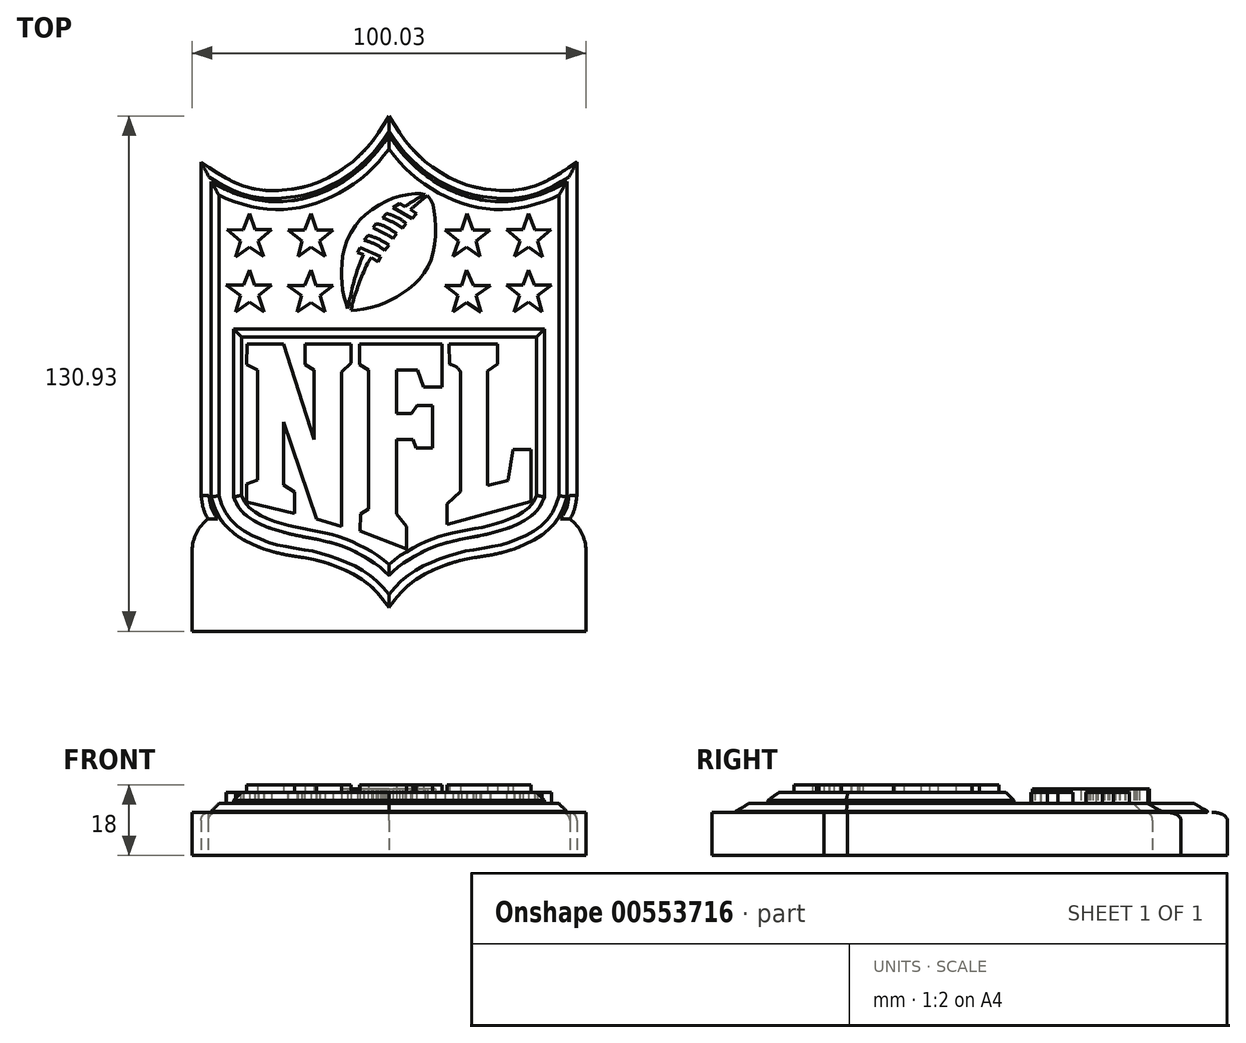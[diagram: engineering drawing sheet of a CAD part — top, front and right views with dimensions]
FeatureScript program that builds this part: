
annotation { "Feature Type Name" : "Feature", "Feature Type Description" : "" }
export const myFeature = defineFeature(function(context is Context, id is Id, definition is map)
    precondition{}
    {
        {
            var Q0;
            Q0=qCreatedBy(makeId("Top.planeOp"),FACE);
            var sketch = newSketch(context, id + "F0", { "sketchPlane" : qUnion([Q0])});
            skLineSegment(sketch, "E0", {"start": v(50, 132.63) * mm, "end": v(50, 0) * mm, "construction": true});
            skLineSegment(sketch, "E1", {"start": v(0, 66.31) * mm, "end": v(100, 66.31) * mm, "construction": true});
            skLineSegment(sketch, "E2", {"start": v(2.28, 119.14) * mm, "end": v(2.28, 34.43) * mm});
            skFitSpline(sketch, "E3", {"points": [v(2.28, 34.43) * mm, v(2.7, 31.8) * mm, v(3.9, 28.8) * mm, v(6.54, 25.06) * mm, v(6.72, 24.8) * mm, v(11.59, 20.83) * mm, v(18.84, 17.77) * mm, v(25.54, 16.2) * mm, v(30.8, 15.28) * mm, v(36.61, 13.45) * mm, v(42.89, 9.8) * mm, v(47.24, 5.22) * mm, v(49.83, 1.28) * mm], "startDerivative": vector(5.68, -43.12) * mm, "endDerivative": vector(28.67, -47.03) * mm});
            skFitSpline(sketch, "E4", {"points": [v(2.28, 119.14) * mm, v(6.14, 116.65) * mm, v(11.7, 113.64) * mm, v(17.48, 112.13) * mm, v(24.37, 112.19) * mm, v(31.61, 113.93) * mm, v(38.21, 117.4) * mm, v(43.13, 121.5) * mm, v(46.78, 125.85) * mm, v(50, 130.93) * mm], "startDerivative": vector(38.47, -25.35) * mm, "endDerivative": vector(28.8, 47.95) * mm});
            skFitSpline(sketch, "E5.MirrorCS", {"points": [v(97.72, 119.14) * mm, v(93.86, 116.65) * mm, v(88.3, 113.64) * mm, v(82.52, 112.13) * mm, v(75.63, 112.19) * mm, v(68.39, 113.93) * mm, v(61.79, 117.4) * mm, v(56.87, 121.5) * mm, v(53.22, 125.85) * mm, v(50, 130.93) * mm], "startDerivative": vector(-38.47, -25.35) * mm, "endDerivative": vector(-28.8, 47.95) * mm});
            skLineSegment(sketch, "E6.MirrorCS", {"start": v(97.72, 119.14) * mm, "end": v(97.72, 34.43) * mm});
            skFitSpline(sketch, "E7.MirrorCS", {"points": [v(97.72, 34.43) * mm, v(97.3, 31.8) * mm, v(96.1, 28.8) * mm, v(93.46, 25.06) * mm, v(93.28, 24.8) * mm, v(88.41, 20.83) * mm, v(81.16, 17.77) * mm, v(74.46, 16.2) * mm, v(69.2, 15.28) * mm, v(63.39, 13.45) * mm, v(57.11, 9.8) * mm, v(52.76, 5.22) * mm, v(50.17, 1.28) * mm], "startDerivative": vector(-5.68, -43.12) * mm, "endDerivative": vector(-28.67, -47.03) * mm});
            skLineSegment(sketch, "E8", {"start": v(49.83, 1.28) * mm, "end": v(50.17, 1.28) * mm});
            skSolve(sketch);
        }
        {
            var Q0;
            Q0=qSketchRegion(id+"F0",true);
            extrude(context, id + "F1", {"entities" : qUnion([Q0]), "depth" : 11 * mm, "offsetDistance" : 25 * mm});
        }
        {
            var Q0;
            Q0=qCreatedBy(makeId("Top.planeOp"),FACE);
            var sketch = newSketch(context, id + "F2", { "sketchPlane" : qUnion([Q0])});
            skLineSegment(sketch, "E9", {"start": v(4.81, 114.27) * mm, "end": v(4.81, 34.15) * mm});
            skFitSpline(sketch, "E10", {"points": [v(4.81, 34.15) * mm, v(5.59, 31.7) * mm, v(7.24, 28.39) * mm, v(9.58, 25.71) * mm, v(13.14, 23.2) * mm, v(19.38, 20.53) * mm, v(25.14, 19.21) * mm, v(30.66, 18.27) * mm, v(36.62, 16.45) * mm, v(42.35, 13.69) * mm, v(46.76, 10.07) * mm, v(50, 6.03) * mm], "startDerivative": vector(10.12, -36.02) * mm, "endDerivative": vector(32.83, -44.73) * mm});
            skFitSpline(sketch, "E11", {"points": [v(4.81, 114.27) * mm, v(9.5, 111.76) * mm, v(18.69, 109.31) * mm, v(27.27, 109.72) * mm, v(36.46, 113.13) * mm, v(44.77, 119.4) * mm, v(49.95, 125.93) * mm], "startDerivative": vector(31.76, -19.44) * mm, "endDerivative": vector(28.45, 40.4) * mm});
            skFitSpline(sketch, "E12.MirrorCS", {"points": [v(95.19, 114.27) * mm, v(90.5, 111.76) * mm, v(81.31, 109.31) * mm, v(72.73, 109.72) * mm, v(63.54, 113.13) * mm, v(55.23, 119.4) * mm, v(50.05, 125.93) * mm], "startDerivative": vector(-31.76, -19.44) * mm, "endDerivative": vector(-28.45, 40.4) * mm});
            skLineSegment(sketch, "E13.MirrorCS", {"start": v(95.19, 114.27) * mm, "end": v(95.19, 34.15) * mm});
            skFitSpline(sketch, "E14.MirrorCS", {"points": [v(95.19, 34.15) * mm, v(94.41, 31.7) * mm, v(92.76, 28.39) * mm, v(90.42, 25.71) * mm, v(86.86, 23.2) * mm, v(80.62, 20.53) * mm, v(74.86, 19.21) * mm, v(69.34, 18.27) * mm, v(63.38, 16.45) * mm, v(57.65, 13.69) * mm, v(53.24, 10.07) * mm, v(50, 6.03) * mm], "startDerivative": vector(-10.12, -36.02) * mm, "endDerivative": vector(-32.83, -44.73) * mm});
            skLineSegment(sketch, "E15", {"start": v(50, 6.03) * mm, "end": v(50, 6.03) * mm});
            skLineSegment(sketch, "E16", {"start": v(49.95, 125.93) * mm, "end": v(50.05, 125.93) * mm});
            skSolve(sketch);
        }
        {
            var Q0;
            Q0=qSketchRegion(id+"F2",true);
            extrude(context, id + "F3", {"entities" : qUnion([Q0]), "operationType" : NewBodyOperationType.ADD, "depth" : 13.2 * mm, "offsetDistance" : 25 * mm});
        }
        {
            var Q0;
            Q0=makeQuery(id+"F1.opExtrude","CAP_EDGE",EDGE,{"disambiguationData":[OSD([sQuery(id+"F0.wireOp",EDGE,"E2")])],"isStart":false});
            var Q1;
            Q1=makeQuery(id+"F1.opExtrude","CAP_EDGE",EDGE,{"disambiguationData":[OSD([sQuery(id+"F0.wireOp",EDGE,"E4")])],"isStart":false});
            var Q2;
            Q2=makeQuery(id+"F1.opExtrude","CAP_EDGE",EDGE,{"disambiguationData":[OSD([sQuery(id+"F0.wireOp",EDGE,"E5.MirrorCS")])],"isStart":false});
            var Q3;
            Q3=makeQuery(id+"F1.opExtrude","CAP_EDGE",EDGE,{"disambiguationData":[OSD([sQuery(id+"F0.wireOp",EDGE,"E6.MirrorCS")])],"isStart":false});
            var Q4;
            Q4=makeQuery(id+"F1.opExtrude","CAP_EDGE",EDGE,{"disambiguationData":[OSD([sQuery(id+"F0.wireOp",EDGE,"E7.MirrorCS")])],"isStart":false});
            var Q5;
            Q5=makeQuery(id+"F1.opExtrude","CAP_EDGE",EDGE,{"disambiguationData":[OSD([sQuery(id+"F0.wireOp",EDGE,"E3")])],"isStart":false});
            fillet(context, id + "F4", {"entities" : qUnion([Q0, Q1, Q2, Q3, Q4, Q5]), "radius" : 2 * mm, "tangentPropagation" : true, "allowEdgeOverflow" : false});
        }
        {
            var Q0;
            Q0=qCreatedBy(makeId("Top.planeOp"),FACE);
            var sketch = newSketch(context, id + "F5", { "sketchPlane" : qUnion([Q0])});
            skLineSegment(sketch, "E17", {"start": v(12.94, 101.93) * mm, "end": v(14.6, 106.09) * mm});
            skLineSegment(sketch, "E18", {"start": v(14.6, 106.09) * mm, "end": v(16, 102) * mm});
            skLineSegment(sketch, "E19", {"start": v(16, 102) * mm, "end": v(20.2, 102) * mm});
            skLineSegment(sketch, "E20", {"start": v(20.2, 102) * mm, "end": v(16.73, 99.2) * mm});
            skLineSegment(sketch, "E21", {"start": v(16.73, 99.2) * mm, "end": v(18.1, 95.2) * mm});
            skLineSegment(sketch, "E22", {"start": v(18.1, 95.2) * mm, "end": v(14.6, 97.61) * mm});
            skLineSegment(sketch, "E23", {"start": v(14.6, 97.61) * mm, "end": v(11.02, 95.08) * mm});
            skLineSegment(sketch, "E24", {"start": v(11.02, 95.08) * mm, "end": v(12.25, 99.2) * mm});
            skLineSegment(sketch, "E25", {"start": v(12.25, 99.2) * mm, "end": v(8.8, 102) * mm});
            skLineSegment(sketch, "E26", {"start": v(8.8, 102) * mm, "end": v(12.94, 101.93) * mm});
            skLineSegment(sketch, "E27", {"start": v(28.6, 101.93) * mm, "end": v(30.15, 106.09) * mm});
            skLineSegment(sketch, "E28", {"start": v(30.15, 106.09) * mm, "end": v(31.57, 101.93) * mm});
            skLineSegment(sketch, "E29", {"start": v(31.57, 101.93) * mm, "end": v(35.75, 101.93) * mm});
            skLineSegment(sketch, "E30", {"start": v(35.75, 101.93) * mm, "end": v(32.38, 99.2) * mm});
            skLineSegment(sketch, "E31", {"start": v(32.38, 99.2) * mm, "end": v(33.75, 95.2) * mm});
            skLineSegment(sketch, "E32", {"start": v(33.75, 95.2) * mm, "end": v(30.26, 97.61) * mm});
            skLineSegment(sketch, "E33", {"start": v(30.26, 97.61) * mm, "end": v(26.9, 95.23) * mm});
            skLineSegment(sketch, "E34", {"start": v(26.9, 95.23) * mm, "end": v(27.86, 99.2) * mm});
            skLineSegment(sketch, "E35", {"start": v(27.86, 99.2) * mm, "end": v(24.4, 101.93) * mm});
            skLineSegment(sketch, "E36", {"start": v(24.4, 101.93) * mm, "end": v(28.6, 101.93) * mm});
            skLineSegment(sketch, "E37", {"start": v(14.6, 91.77) * mm, "end": v(15.9, 87.96) * mm});
            skLineSegment(sketch, "E38", {"start": v(15.9, 87.96) * mm, "end": v(20.12, 87.96) * mm});
            skLineSegment(sketch, "E39", {"start": v(20.12, 87.96) * mm, "end": v(16.82, 85.26) * mm});
            skLineSegment(sketch, "E40", {"start": v(16.82, 85.26) * mm, "end": v(18.25, 81.05) * mm});
            skLineSegment(sketch, "E41", {"start": v(18.25, 81.05) * mm, "end": v(14.6, 83.58) * mm});
            skLineSegment(sketch, "E42", {"start": v(14.6, 83.58) * mm, "end": v(11.08, 81.12) * mm});
            skLineSegment(sketch, "E43", {"start": v(11.08, 81.12) * mm, "end": v(12.33, 85.26) * mm});
            skLineSegment(sketch, "E44", {"start": v(12.33, 85.26) * mm, "end": v(8.66, 87.96) * mm});
            skLineSegment(sketch, "E45", {"start": v(8.66, 87.96) * mm, "end": v(13, 87.96) * mm});
            skLineSegment(sketch, "E46", {"start": v(13, 87.96) * mm, "end": v(14.6, 91.77) * mm});
            skLineSegment(sketch, "E47", {"start": v(30.26, 91.71) * mm, "end": v(31.53, 87.83) * mm});
            skLineSegment(sketch, "E48", {"start": v(31.53, 87.83) * mm, "end": v(35.8, 87.83) * mm});
            skLineSegment(sketch, "E49", {"start": v(35.8, 87.83) * mm, "end": v(32.42, 85.26) * mm});
            skLineSegment(sketch, "E50", {"start": v(32.42, 85.26) * mm, "end": v(33.78, 81.05) * mm});
            skLineSegment(sketch, "E51", {"start": v(33.78, 81.05) * mm, "end": v(30.26, 83.49) * mm});
            skLineSegment(sketch, "E52", {"start": v(30.26, 83.49) * mm, "end": v(26.68, 81.07) * mm});
            skLineSegment(sketch, "E53", {"start": v(26.68, 81.07) * mm, "end": v(27.84, 85.26) * mm});
            skLineSegment(sketch, "E54", {"start": v(27.84, 85.26) * mm, "end": v(24.2, 87.79) * mm});
            skLineSegment(sketch, "E55", {"start": v(24.2, 87.79) * mm, "end": v(28.58, 87.79) * mm});
            skLineSegment(sketch, "E56", {"start": v(28.58, 87.79) * mm, "end": v(30.26, 91.71) * mm});
            skLineSegment(sketch, "E57.MirrorCS", {"start": v(69.74, 91.71) * mm, "end": v(68.47, 87.83) * mm});
            skLineSegment(sketch, "E58.MirrorCS", {"start": v(68.47, 87.83) * mm, "end": v(64.2, 87.83) * mm});
            skLineSegment(sketch, "E59.MirrorCS", {"start": v(64.2, 87.83) * mm, "end": v(67.58, 85.26) * mm});
            skLineSegment(sketch, "E60.MirrorCS", {"start": v(67.58, 85.26) * mm, "end": v(66.22, 81.05) * mm});
            skLineSegment(sketch, "E61.MirrorCS", {"start": v(66.22, 81.05) * mm, "end": v(69.74, 83.49) * mm});
            skLineSegment(sketch, "E62.MirrorCS", {"start": v(69.74, 83.49) * mm, "end": v(73.32, 81.07) * mm});
            skLineSegment(sketch, "E63.MirrorCS", {"start": v(73.32, 81.07) * mm, "end": v(72.16, 85.26) * mm});
            skLineSegment(sketch, "E64.MirrorCS", {"start": v(72.16, 85.26) * mm, "end": v(75.8, 87.79) * mm});
            skLineSegment(sketch, "E65.MirrorCS", {"start": v(75.8, 87.79) * mm, "end": v(71.42, 87.79) * mm});
            skLineSegment(sketch, "E66.MirrorCS", {"start": v(71.42, 87.79) * mm, "end": v(69.74, 91.71) * mm});
            skLineSegment(sketch, "E67.MirrorCS", {"start": v(69.85, 106.09) * mm, "end": v(68.43, 101.93) * mm});
            skLineSegment(sketch, "E68.MirrorCS", {"start": v(71.4, 101.93) * mm, "end": v(69.85, 106.09) * mm});
            skLineSegment(sketch, "E69.MirrorCS", {"start": v(75.6, 101.93) * mm, "end": v(71.4, 101.93) * mm});
            skLineSegment(sketch, "E70.MirrorCS", {"start": v(72.14, 99.2) * mm, "end": v(75.6, 101.93) * mm});
            skLineSegment(sketch, "E71.MirrorCS", {"start": v(73.1, 95.23) * mm, "end": v(72.14, 99.2) * mm});
            skLineSegment(sketch, "E72.MirrorCS", {"start": v(69.74, 97.61) * mm, "end": v(73.1, 95.23) * mm});
            skLineSegment(sketch, "E73.MirrorCS", {"start": v(66.25, 95.2) * mm, "end": v(69.74, 97.61) * mm});
            skLineSegment(sketch, "E74.MirrorCS", {"start": v(67.62, 99.2) * mm, "end": v(66.25, 95.2) * mm});
            skLineSegment(sketch, "E75.MirrorCS", {"start": v(64.25, 101.93) * mm, "end": v(67.62, 99.2) * mm});
            skLineSegment(sketch, "E76.MirrorCS", {"start": v(68.43, 101.93) * mm, "end": v(64.25, 101.93) * mm});
            skLineSegment(sketch, "E77.MirrorCS", {"start": v(85.4, 106.09) * mm, "end": v(84, 102) * mm});
            skLineSegment(sketch, "E78.MirrorCS", {"start": v(87.06, 101.93) * mm, "end": v(85.4, 106.09) * mm});
            skLineSegment(sketch, "E79.MirrorCS", {"start": v(91.2, 102) * mm, "end": v(87.06, 101.93) * mm});
            skLineSegment(sketch, "E80.MirrorCS", {"start": v(87.75, 99.2) * mm, "end": v(91.2, 102) * mm});
            skLineSegment(sketch, "E81.MirrorCS", {"start": v(88.98, 95.08) * mm, "end": v(87.75, 99.2) * mm});
            skLineSegment(sketch, "E82.MirrorCS", {"start": v(85.4, 97.61) * mm, "end": v(88.98, 95.08) * mm});
            skLineSegment(sketch, "E83.MirrorCS", {"start": v(81.9, 95.2) * mm, "end": v(85.4, 97.61) * mm});
            skLineSegment(sketch, "E84.MirrorCS", {"start": v(83.27, 99.2) * mm, "end": v(81.9, 95.2) * mm});
            skLineSegment(sketch, "E85.MirrorCS", {"start": v(79.8, 102) * mm, "end": v(83.27, 99.2) * mm});
            skLineSegment(sketch, "E86.MirrorCS", {"start": v(84, 102) * mm, "end": v(79.8, 102) * mm});
            skLineSegment(sketch, "E87.MirrorCS", {"start": v(85.4, 91.77) * mm, "end": v(84.1, 87.96) * mm});
            skLineSegment(sketch, "E88.MirrorCS", {"start": v(87, 87.96) * mm, "end": v(85.4, 91.77) * mm});
            skLineSegment(sketch, "E89.MirrorCS", {"start": v(91.34, 87.96) * mm, "end": v(87, 87.96) * mm});
            skLineSegment(sketch, "E90.MirrorCS", {"start": v(87.67, 85.26) * mm, "end": v(91.34, 87.96) * mm});
            skLineSegment(sketch, "E91.MirrorCS", {"start": v(88.92, 81.12) * mm, "end": v(87.67, 85.26) * mm});
            skLineSegment(sketch, "E92.MirrorCS", {"start": v(85.4, 83.58) * mm, "end": v(88.92, 81.12) * mm});
            skLineSegment(sketch, "E93.MirrorCS", {"start": v(81.75, 81.05) * mm, "end": v(85.4, 83.58) * mm});
            skLineSegment(sketch, "E94.MirrorCS", {"start": v(83.18, 85.26) * mm, "end": v(81.75, 81.05) * mm});
            skLineSegment(sketch, "E95.MirrorCS", {"start": v(79.88, 87.96) * mm, "end": v(83.18, 85.26) * mm});
            skLineSegment(sketch, "E96.MirrorCS", {"start": v(84.1, 87.96) * mm, "end": v(79.88, 87.96) * mm});
            skLineSegment(sketch, "E97", {"start": v(10.5, 76.74) * mm, "end": v(49.97, 76.74) * mm});
            skPoint(sketch, "E97.startSnap0", {"position": v(10.5, 86.61) * mm});
            skLineSegment(sketch, "E98", {"start": v(10.5, 76.74) * mm, "end": v(10.5, 34.11) * mm});
            skFitSpline(sketch, "E99", {"points": [v(10.5, 34.11) * mm, v(12.27, 30.84) * mm, v(16.58, 27.57) * mm, v(24.85, 24.72) * mm, v(31.63, 23.36) * mm, v(39.01, 21.26) * mm, v(46.72, 17.05) * mm, v(49.97, 14.22) * mm], "startDerivative": vector(13.37, -30.84) * mm, "endDerivative": vector(23.65, -23.25) * mm});
            skLineSegment(sketch, "E100.MirrorCS", {"start": v(89.5, 76.74) * mm, "end": v(50.03, 76.74) * mm});
            skLineSegment(sketch, "E101.MirrorCS", {"start": v(89.5, 76.74) * mm, "end": v(89.5, 34.11) * mm});
            skFitSpline(sketch, "E102.MirrorCS", {"points": [v(89.5, 34.11) * mm, v(87.73, 30.84) * mm, v(83.42, 27.57) * mm, v(75.15, 24.72) * mm, v(68.37, 23.36) * mm, v(60.99, 21.26) * mm, v(53.28, 17.05) * mm, v(50.03, 14.22) * mm], "startDerivative": vector(-13.37, -30.84) * mm, "endDerivative": vector(-23.65, -23.25) * mm});
            skLineSegment(sketch, "E103", {"start": v(49.97, 14.22) * mm, "end": v(50.03, 14.22) * mm});
            skLineSegment(sketch, "E104", {"start": v(49.97, 76.74) * mm, "end": v(50.03, 76.74) * mm});
            skSolve(sketch);
        }
        {
            var Q0;
            Q0=qSketchRegion(id+"F5",true);
            extrude(context, id + "F6", {"entities" : qUnion([Q0]), "operationType" : NewBodyOperationType.ADD, "depth" : 16 * mm, "offsetDistance" : 25 * mm});
        }
        {
            var Q0;
            Q0=makeQuery(id+"F6.opExtrude","CAP_EDGE",EDGE,{"disambiguationData":[OSD([sQuery(id+"F5.wireOp",EDGE,"E99")])],"isStart":false});
            var Q1;
            Q1=makeQuery(id+"F6.opExtrude","CAP_EDGE",EDGE,{"disambiguationData":[OSD([sQuery(id+"F5.wireOp",EDGE,"E102.MirrorCS")])],"isStart":false});
            var Q2;
            Q2=makeQuery(id+"F6.opExtrude","CAP_EDGE",EDGE,{"disambiguationData":[OSD([sQuery(id+"F5.wireOp",EDGE,"E101.MirrorCS")])],"isStart":false});
            var Q3;
            Q3=makeQuery(id+"F6.opExtrude","CAP_EDGE",EDGE,{"disambiguationData":[OSD([sQuery(id+"F5.wireOp",EDGE,"E97"),sQuery(id+"F5.wireOp",EDGE,"E100.MirrorCS"),sQuery(id+"F5.wireOp",EDGE,"E104")])],"isStart":false});
            var Q4;
            Q4=makeQuery(id+"F6.opExtrude","CAP_EDGE",EDGE,{"disambiguationData":[OSD([sQuery(id+"F5.wireOp",EDGE,"E98")])],"isStart":false});
            chamfer(context, id + "F7", {"entities" : qUnion([Q0, Q1, Q2, Q3, Q4]), "width" : 2 * mm, "tangentPropagation" : true});
        }
        {
            var Q0;
            Q0=makeQuery(id+"F3.opExtrude","CAP_EDGE",EDGE,{"disambiguationData":[OSD([sQuery(id+"F2.wireOp",EDGE,"E9")])],"isStart":false});
            var Q1;
            Q1=makeQuery(id+"F3.opExtrude","CAP_EDGE",EDGE,{"disambiguationData":[OSD([sQuery(id+"F2.wireOp",EDGE,"E11")])],"isStart":false});
            var Q2;
            Q2=makeQuery(id+"F3.opExtrude","CAP_EDGE",EDGE,{"disambiguationData":[OSD([sQuery(id+"F2.wireOp",EDGE,"E12.MirrorCS")])],"isStart":false});
            var Q3;
            Q3=makeQuery(id+"F3.opExtrude","CAP_EDGE",EDGE,{"disambiguationData":[OSD([sQuery(id+"F2.wireOp",EDGE,"E13.MirrorCS")])],"isStart":false});
            var Q4;
            Q4=makeQuery(id+"F3.opExtrude","CAP_EDGE",EDGE,{"disambiguationData":[OSD([sQuery(id+"F2.wireOp",EDGE,"E14.MirrorCS")])],"isStart":false});
            var Q5;
            Q5=makeQuery(id+"F3.opExtrude","CAP_EDGE",EDGE,{"disambiguationData":[OSD([sQuery(id+"F2.wireOp",EDGE,"E10")])],"isStart":false});
            chamfer(context, id + "F8", {"entities" : qUnion([Q0, Q1, Q2, Q3, Q4, Q5]), "width" : 2 * mm, "tangentPropagation" : true});
        }
        {
            var Q0;
            Q0=qCreatedBy(makeId("Top.planeOp"),FACE);
            var sketch = newSketch(context, id + "F9", { "sketchPlane" : qUnion([Q0])});
            skLineSegment(sketch, "E105", {"start": v(13.9, 72.92) * mm, "end": v(23.18, 72.92) * mm});
            skLineSegment(sketch, "E106", {"start": v(23.18, 72.92) * mm, "end": v(31, 48.74) * mm});
            skLineSegment(sketch, "E107", {"start": v(31, 48.74) * mm, "end": v(31, 66.35) * mm});
            skLineSegment(sketch, "E108", {"start": v(31, 66.35) * mm, "end": v(28.72, 67.8) * mm});
            skLineSegment(sketch, "E109", {"start": v(28.72, 67.8) * mm, "end": v(28.72, 72.92) * mm});
            skLineSegment(sketch, "E110", {"start": v(28.72, 72.92) * mm, "end": v(40.37, 72.92) * mm});
            skLineSegment(sketch, "E111", {"start": v(40.37, 72.92) * mm, "end": v(40.37, 68.16) * mm});
            skLineSegment(sketch, "E112", {"start": v(40.37, 68.16) * mm, "end": v(37.99, 65.82) * mm});
            skLineSegment(sketch, "E113", {"start": v(37.99, 65.82) * mm, "end": v(37.99, 26.65) * mm});
            skLineSegment(sketch, "E114", {"start": v(37.99, 26.65) * mm, "end": v(31.63, 28.46) * mm});
            skLineSegment(sketch, "E115", {"start": v(31.63, 28.46) * mm, "end": v(23.18, 53.12) * mm});
            skLineSegment(sketch, "E116", {"start": v(23.18, 53.12) * mm, "end": v(23.18, 37.14) * mm});
            skLineSegment(sketch, "E117", {"start": v(23.18, 37.14) * mm, "end": v(26.03, 35.33) * mm});
            skLineSegment(sketch, "E118", {"start": v(26.03, 35.33) * mm, "end": v(26.03, 29.88) * mm});
            skLineSegment(sketch, "E119", {"start": v(26.03, 29.88) * mm, "end": v(13.8, 32.88) * mm});
            skLineSegment(sketch, "E120", {"start": v(13.8, 32.88) * mm, "end": v(13.8, 37.43) * mm});
            skLineSegment(sketch, "E121", {"start": v(13.8, 37.43) * mm, "end": v(16.56, 38.38) * mm});
            skLineSegment(sketch, "E122", {"start": v(16.56, 38.38) * mm, "end": v(16.56, 66.35) * mm});
            skLineSegment(sketch, "E123", {"start": v(16.56, 66.35) * mm, "end": v(13.87, 67.8) * mm});
            skLineSegment(sketch, "E124", {"start": v(13.87, 67.8) * mm, "end": v(13.9, 72.92) * mm});
            skLineSegment(sketch, "E125", {"start": v(42.63, 25.5) * mm, "end": v(54.44, 20.86) * mm});
            skLineSegment(sketch, "E126", {"start": v(54.44, 20.86) * mm, "end": v(54.44, 26.6) * mm});
            skLineSegment(sketch, "E127", {"start": v(54.44, 26.6) * mm, "end": v(51.92, 29.8) * mm});
            skLineSegment(sketch, "E128", {"start": v(51.92, 29.8) * mm, "end": v(51.92, 48.74) * mm});
            skLineSegment(sketch, "E129", {"start": v(51.92, 48.74) * mm, "end": v(56.17, 48.74) * mm});
            skLineSegment(sketch, "E130", {"start": v(56.17, 48.74) * mm, "end": v(56.92, 46.54) * mm});
            skLineSegment(sketch, "E131", {"start": v(56.92, 46.54) * mm, "end": v(61, 46.54) * mm});
            skLineSegment(sketch, "E132", {"start": v(61, 46.54) * mm, "end": v(61, 57.37) * mm});
            skLineSegment(sketch, "E133", {"start": v(61, 57.37) * mm, "end": v(57.1, 57.37) * mm});
            skLineSegment(sketch, "E134", {"start": v(57.1, 57.37) * mm, "end": v(55.79, 55.3) * mm});
            skLineSegment(sketch, "E135", {"start": v(55.79, 55.3) * mm, "end": v(51.92, 55.3) * mm});
            skLineSegment(sketch, "E136", {"start": v(51.92, 55.3) * mm, "end": v(51.92, 66.35) * mm});
            skLineSegment(sketch, "E137", {"start": v(51.92, 66.35) * mm, "end": v(57.3, 66.35) * mm});
            skLineSegment(sketch, "E138", {"start": v(57.3, 66.35) * mm, "end": v(58.8, 62) * mm});
            skLineSegment(sketch, "E139", {"start": v(58.8, 62) * mm, "end": v(63.48, 62) * mm});
            skLineSegment(sketch, "E140", {"start": v(63.48, 62) * mm, "end": v(63.48, 72.92) * mm});
            skLineSegment(sketch, "E141", {"start": v(63.48, 72.92) * mm, "end": v(42.48, 72.92) * mm});
            skLineSegment(sketch, "E142", {"start": v(42.48, 72.92) * mm, "end": v(42.48, 67.8) * mm});
            skLineSegment(sketch, "E143", {"start": v(42.48, 67.8) * mm, "end": v(44.76, 66.35) * mm});
            skLineSegment(sketch, "E144", {"start": v(44.76, 66.35) * mm, "end": v(44.76, 31.04) * mm});
            skLineSegment(sketch, "E145", {"start": v(44.76, 31.04) * mm, "end": v(42.73, 29.8) * mm});
            skLineSegment(sketch, "E146", {"start": v(42.73, 29.8) * mm, "end": v(42.63, 25.5) * mm});
            skLineSegment(sketch, "E147", {"start": v(65.3, 72.92) * mm, "end": v(77.57, 72.92) * mm});
            skLineSegment(sketch, "E148", {"start": v(77.57, 72.92) * mm, "end": v(77.57, 67.95) * mm});
            skLineSegment(sketch, "E149", {"start": v(77.57, 67.95) * mm, "end": v(75.02, 66.06) * mm});
            skLineSegment(sketch, "E150", {"start": v(75.02, 66.06) * mm, "end": v(75.02, 37) * mm});
            skLineSegment(sketch, "E151", {"start": v(75.02, 37) * mm, "end": v(80.23, 38.32) * mm});
            skLineSegment(sketch, "E152", {"start": v(80.23, 38.32) * mm, "end": v(81.55, 46.18) * mm});
            skLineSegment(sketch, "E153", {"start": v(81.55, 46.18) * mm, "end": v(86.1, 46.18) * mm});
            skLineSegment(sketch, "E154", {"start": v(86.1, 46.18) * mm, "end": v(86.1, 32.98) * mm});
            skLineSegment(sketch, "E155", {"start": v(86.1, 32.98) * mm, "end": v(64.71, 27.14) * mm});
            skLineSegment(sketch, "E156", {"start": v(64.71, 27.14) * mm, "end": v(64.71, 32.35) * mm});
            skLineSegment(sketch, "E157", {"start": v(64.71, 32.35) * mm, "end": v(68.14, 35.5) * mm});
            skLineSegment(sketch, "E158", {"start": v(68.14, 35.5) * mm, "end": v(68.14, 65.96) * mm});
            skFitSpline(sketch, "E159", {"points": [v(68.14, 65.96) * mm, v(67.23, 67.08) * mm, v(65.34, 67.88) * mm], "startDerivative": vector(-1.66, 2.67) * mm, "endDerivative": vector(-3.87, 1.21) * mm});
            skLineSegment(sketch, "E160", {"start": v(65.3, 72.92) * mm, "end": v(65.34, 67.88) * mm});
            skSolve(sketch);
        }
        {
            var Q0;
            Q0=qSketchRegion(id+"F9",true);
            extrude(context, id + "F10", {"entities" : qUnion([Q0]), "operationType" : NewBodyOperationType.ADD, "depth" : 18 * mm, "offsetDistance" : 25 * mm});
        }
        {
            var Q0;
            Q0=qCreatedBy(makeId("Top.planeOp"),FACE);
            var sketch = newSketch(context, id + "F11", { "sketchPlane" : qUnion([Q0])});
            skFitSpline(sketch, "E161", {"points": [v(40.4, 81.47) * mm, v(43.64, 81.93) * mm, v(47.96, 83.03) * mm, v(51.35, 84.6) * mm, v(54.88, 86.88) * mm, v(58.2, 90.03) * mm, v(60.5, 93.9) * mm, v(61.7, 98.88) * mm, v(61.7, 105.22) * mm, v(60.98, 108.78) * mm, v(59.83, 110.73) * mm], "startDerivative": vector(34.78, 4.2) * mm, "endDerivative": vector(-17.03, 24.47) * mm});
            skFitSpline(sketch, "E162", {"points": [v(59.83, 110.73) * mm, v(58.32, 109.56) * mm, v(55.47, 107.17) * mm], "startDerivative": vector(-3.35, -2.53) * mm, "endDerivative": vector(-5.27, -4.48) * mm});
            skLineSegment(sketch, "E163", {"start": v(55.47, 107.17) * mm, "end": v(56.95, 106.08) * mm});
            skLineSegment(sketch, "E164", {"start": v(56.95, 106.08) * mm, "end": v(55.8, 104.9) * mm});
            skLineSegment(sketch, "E165", {"start": v(55.8, 104.9) * mm, "end": v(51.08, 107.59) * mm});
            skLineSegment(sketch, "E166", {"start": v(51.08, 107.59) * mm, "end": v(52.72, 108.6) * mm});
            skLineSegment(sketch, "E167", {"start": v(52.72, 108.6) * mm, "end": v(54.09, 107.94) * mm});
            skFitSpline(sketch, "E168", {"points": [v(54.09, 107.94) * mm, v(55.1, 108.62) * mm, v(56.61, 109.57) * mm, v(58.02, 110.34) * mm, v(59.16, 110.89) * mm], "startDerivative": vector(4.18, 2.82) * mm, "endDerivative": vector(4.83, 2.25) * mm});
            skFitSpline(sketch, "E169", {"points": [v(59.16, 110.89) * mm, v(58, 111.15) * mm, v(55.9, 111.13) * mm, v(52.2, 110.4) * mm, v(49.4, 109.35) * mm, v(45.9, 107.33) * mm, v(43.07, 104.97) * mm, v(40.87, 102.22) * mm, v(39.03, 98.4) * mm, v(38.15, 94.47) * mm, v(37.98, 91.66) * mm, v(37.97, 89.4) * mm, v(38.28, 86.5) * mm, v(38.93, 83.84) * mm, v(39.53, 82.04) * mm], "startDerivative": vector(-24.05, 6.94) * mm, "endDerivative": vector(10.62, -29.86) * mm});
            skFitSpline(sketch, "E170", {"points": [v(39.53, 82.04) * mm, v(39.85, 83.57) * mm, v(40.5, 86.5) * mm, v(41.35, 89.84) * mm, v(42.48, 93.2) * mm, v(43.52, 95.66) * mm], "startDerivative": vector(1.86, 9.38) * mm, "endDerivative": vector(5.32, 12) * mm});
            skLineSegment(sketch, "E171", {"start": v(43.52, 95.66) * mm, "end": v(42.01, 96.22) * mm});
            skLineSegment(sketch, "E172", {"start": v(42.01, 96.22) * mm, "end": v(42.65, 97.5) * mm});
            skLineSegment(sketch, "E173", {"start": v(42.65, 97.5) * mm, "end": v(47.9, 95.21) * mm});
            skLineSegment(sketch, "E174", {"start": v(47.9, 95.21) * mm, "end": v(47.27, 93.76) * mm});
            skLineSegment(sketch, "E175", {"start": v(47.27, 93.76) * mm, "end": v(45.55, 94.9) * mm});
            skFitSpline(sketch, "E176", {"points": [v(45.55, 94.9) * mm, v(45, 94.17) * mm, v(43.75, 91.71) * mm, v(42.51, 88.77) * mm, v(41.5, 85.84) * mm, v(40.75, 83.44) * mm, v(40.4, 81.47) * mm], "startDerivative": vector(-4.99, -5.73) * mm, "endDerivative": vector(-1.76, -12.6) * mm});
            skLineSegment(sketch, "E177", {"start": v(43.67, 99.4) * mm, "end": v(44.64, 100.57) * mm});
            skFitSpline(sketch, "E178", {"points": [v(44.64, 100.57) * mm, v(45.63, 100.33) * mm, v(47.1, 99.76) * mm, v(48.96, 98.75) * mm, v(49.97, 98.1) * mm], "startDerivative": vector(4.55, -0.99) * mm, "endDerivative": vector(4, -2.73) * mm});
            skLineSegment(sketch, "E179", {"start": v(49.97, 98.1) * mm, "end": v(48.87, 96.77) * mm});
            skFitSpline(sketch, "E180", {"points": [v(43.67, 99.4) * mm, v(44.96, 98.98) * mm, v(46.26, 98.47) * mm, v(47.43, 97.87) * mm, v(48.44, 97.1) * mm, v(48.87, 96.77) * mm], "startDerivative": vector(5.88, -1.93) * mm, "endDerivative": vector(2.82, -2.08) * mm});
            skLineSegment(sketch, "E181", {"start": v(45.94, 102.57) * mm, "end": v(46.76, 103.54) * mm});
            skFitSpline(sketch, "E182", {"points": [v(46.76, 103.54) * mm, v(47.55, 103.38) * mm, v(48.73, 102.94) * mm, v(49.87, 102.36) * mm, v(51.1, 101.57) * mm, v(51.95, 101) * mm], "startDerivative": vector(4.47, -0.73) * mm, "endDerivative": vector(4.24, -2.87) * mm});
            skLineSegment(sketch, "E183", {"start": v(51.95, 101) * mm, "end": v(51.03, 99.75) * mm});
            skFitSpline(sketch, "E184", {"points": [v(45.94, 102.57) * mm, v(47.35, 101.86) * mm, v(49.1, 100.95) * mm, v(50.07, 100.42) * mm, v(51.03, 99.75) * mm], "startDerivative": vector(5.1, -2.53) * mm, "endDerivative": vector(4.33, -3.17) * mm});
            skLineSegment(sketch, "E185", {"start": v(48.37, 105.01) * mm, "end": v(49.4, 106.16) * mm});
            skFitSpline(sketch, "E186", {"points": [v(49.4, 106.16) * mm, v(50.36, 105.83) * mm, v(51.75, 105.26) * mm, v(53.04, 104.6) * mm, v(54.33, 103.63) * mm], "startDerivative": vector(4.27, -1.42) * mm, "endDerivative": vector(4.73, -3.82) * mm});
            skLineSegment(sketch, "E187", {"start": v(54.33, 103.63) * mm, "end": v(53.4, 102.46) * mm});
            skFitSpline(sketch, "E188", {"points": [v(48.37, 105.01) * mm, v(49.44, 104.6) * mm, v(50.64, 104.08) * mm, v(51.8, 103.54) * mm, v(52.6, 103.03) * mm, v(53.4, 102.46) * mm], "startDerivative": vector(5.3, -1.91) * mm, "endDerivative": vector(4.41, -3.08) * mm});
            skSolve(sketch);
        }
        {
            var Q0;
            Q0=qSketchRegion(id+"F11",true);
            extrude(context, id + "F12", {"entities" : qUnion([Q0]), "operationType" : NewBodyOperationType.ADD, "depth" : 17 * mm, "offsetDistance" : 25 * mm});
        }
        {
            var Q0;
            Q0=qCreatedBy(makeId("Top.planeOp"),FACE);
            var sketch = newSketch(context, id + "F13", { "sketchPlane" : qUnion([Q0])});
            skLineSegment(sketch, "E189.bottom", {"start": v(0, 28.52) * mm, "end": v(100.03, 28.52) * mm});
            skLineSegment(sketch, "E189.top", {"start": v(0, 0) * mm, "end": v(100.03, 0) * mm});
            skLineSegment(sketch, "E189.left", {"start": v(0, 28.52) * mm, "end": v(0, 0) * mm});
            skLineSegment(sketch, "E189.right", {"start": v(100.03, 28.52) * mm, "end": v(100.03, 0) * mm});
            skSolve(sketch);
        }
        {
            var Q0;
            Q0=qSketchRegion(id+"F13",true);
            extrude(context, id + "F14", {"entities" : qUnion([Q0]), "operationType" : NewBodyOperationType.ADD, "depth" : 11 * mm, "offsetDistance" : 25 * mm});
        }
        {
            var Q0;
            Q0=makeQuery(id+"F14.opExtrude","SWEPT_EDGE",EDGE,{"disambiguationData":[OSD([sQuery(id+"F13.wireOp",EDGE,"E189.bottom"),sQuery(id+"F13.wireOp",EDGE,"E189.left")])]});
            fillet(context, id + "F15", {"entities" : qUnion([Q0]), "radius" : 10 * mm, "tangentPropagation" : true, "allowEdgeOverflow" : false});
        }
        {
            var Q0;
            Q0=makeQuery(id+"F14.opExtrude","SWEPT_EDGE",EDGE,{"disambiguationData":[OSD([sQuery(id+"F13.wireOp",EDGE,"E189.bottom"),sQuery(id+"F13.wireOp",EDGE,"E189.right")])]});
            fillet(context, id + "F16", {"entities" : qUnion([Q0]), "radius" : 10 * mm, "tangentPropagation" : true, "allowEdgeOverflow" : false});
        }
    });
